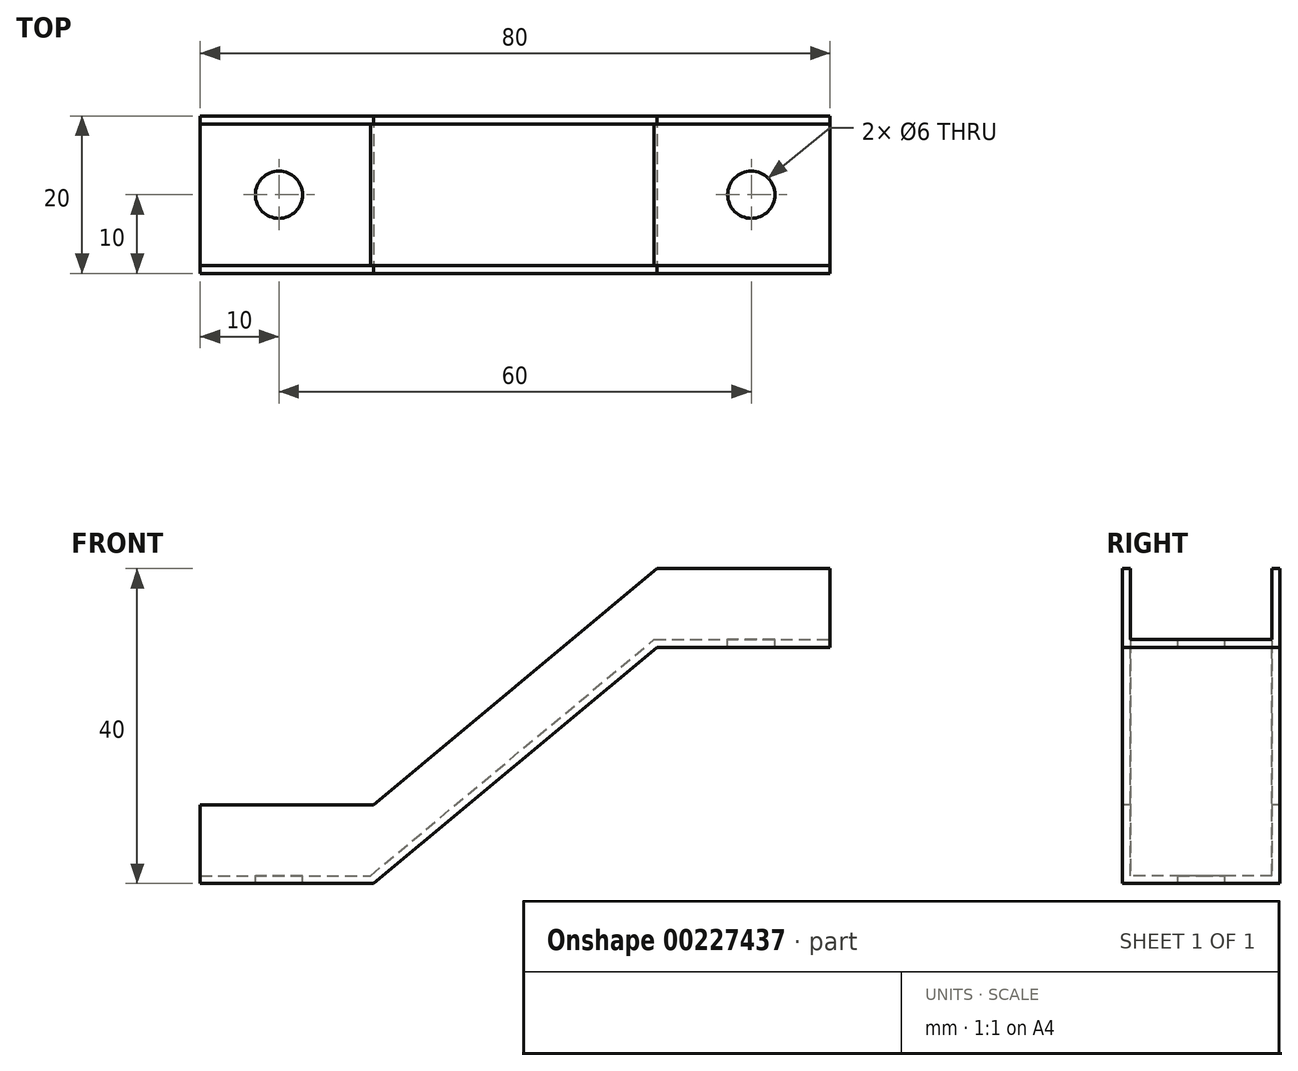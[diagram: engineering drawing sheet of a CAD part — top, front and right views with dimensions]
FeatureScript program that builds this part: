
annotation { "Feature Type Name" : "Feature", "Feature Type Description" : "" }
export const myFeature = defineFeature(function(context is Context, id is Id, definition is map)
    precondition{}
    {
        {
            var Q0;
            Q0=qCreatedBy(makeId("Front.planeOp"),FACE);
            var sketch = newSketch(context, id + "F0", { "sketchPlane" : qUnion([Q0])});
            skLineSegment(sketch, "E0", {"start": v(70, 40) * mm, "end": v(48, 40) * mm});
            skLineSegment(sketch, "E1", {"start": v(48, 40) * mm, "end": v(12, 10) * mm});
            skLineSegment(sketch, "E2", {"start": v(12, 10) * mm, "end": v(-10, 10) * mm});
            skLineSegment(sketch, "E3", {"start": v(-10, 10) * mm, "end": v(-10, 0) * mm});
            skLineSegment(sketch, "E4", {"start": v(-10, 0) * mm, "end": v(12, 0) * mm});
            skLineSegment(sketch, "E5", {"start": v(12, 0) * mm, "end": v(48, 30) * mm});
            skLineSegment(sketch, "E6", {"start": v(48, 30) * mm, "end": v(70, 30) * mm});
            skLineSegment(sketch, "E7", {"start": v(70, 30) * mm, "end": v(70, 40) * mm});
            skLineSegment(sketch, "E8", {"start": v(60, 24.38) * mm, "end": v(60, 43.33) * mm, "construction": true});
            skSolve(sketch);
        }
        {
            var Q0;
            Q0 = qSketchRegion(id + "F0", true);
            extrude(context, id + "F1", {"entities" : qUnion([Q0]), "oppositeDirection" : true, "depth" : 20 * mm});
        }
        {
            var Q0;
            Q0=makeQuery(id+"F1.opExtrude","SWEPT_FACE",FACE,{"disambiguationData":[OSD([sQuery(id+"F0.wireOp",EDGE,"E0")])]});
            var Q1;
            Q1=makeQuery(id+"F1.opExtrude","SWEPT_FACE",FACE,{"disambiguationData":[OSD([sQuery(id+"F0.wireOp",EDGE,"E1")])]});
            var Q2;
            Q2=makeQuery(id+"F1.opExtrude","SWEPT_FACE",FACE,{"disambiguationData":[OSD([sQuery(id+"F0.wireOp",EDGE,"E2")])]});
            var Q3;
            Q3=makeQuery(id+"F1.opExtrude","SWEPT_FACE",FACE,{"disambiguationData":[OSD([sQuery(id+"F0.wireOp",EDGE,"E7")])]});
            var Q4;
            Q4=makeQuery(id+"F1.opExtrude","SWEPT_FACE",FACE,{"disambiguationData":[OSD([sQuery(id+"F0.wireOp",EDGE,"E3")])]});
            shell(context, id + "F2", {"entities" : qUnion([Q0, Q1, Q2, Q3, Q4]), "thickness" : 1 * mm});
        }
        {
            var Q0;
            Q0=makeQuery(id+"F2.opShell","OFFSET_FACE",FACE,{"disambiguationData":[OSD([sQuery(id+"F0.wireOp",EDGE,"E4")])]});
            var sketch = newSketch(context, id + "F3", { "sketchPlane" : qUnion([Q0])});
            skCircle(sketch, "E9", {"center": v(0, 10) * mm, "radius": 3 * mm});
            skSolve(sketch);
        }
        {
            var Q0;
            Q0 = qSketchRegion(id + "F3", true);
            extrude(context, id + "F4", {"entities" : qUnion([Q0]), "operationType" : NewBodyOperationType.REMOVE, "endBound" : BoundingType.THROUGH_ALL, "oppositeDirection" : true, "depth" : 31.84 * mm});
        }
        {
            var Q0;
            Q0=makeQuery(id+"F2.opShell","OFFSET_FACE",FACE,{"disambiguationData":[OSD([sQuery(id+"F0.wireOp",EDGE,"E6")])]});
            var sketch = newSketch(context, id + "F5", { "sketchPlane" : qUnion([Q0])});
            skCircle(sketch, "E10", {"center": v(60, 10) * mm, "radius": 3 * mm});
            skSolve(sketch);
        }
        {
            var Q0;
            Q0 = qSketchRegion(id + "F5", true);
            extrude(context, id + "F6", {"entities" : qUnion([Q0]), "operationType" : NewBodyOperationType.REMOVE, "endBound" : BoundingType.THROUGH_ALL, "oppositeDirection" : true, "depth" : 11.26 * mm});
        }
    });
